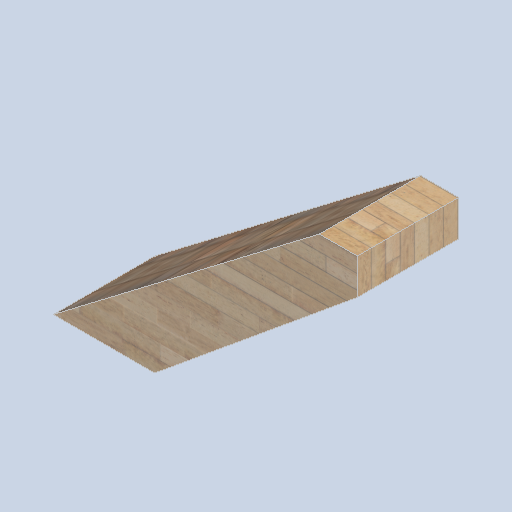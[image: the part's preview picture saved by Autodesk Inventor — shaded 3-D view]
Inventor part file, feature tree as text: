
AUTODESK INVENTOR PART (.ipt)
format: ipt  version: 2024.2 (Build 282272000, 272)  size: 160,256 bytes
history: native  units: in
note: dims shown in document units (in); Inventor stores cm internally (conversion verified against a paired STEP export)
features: other x3, sketch x1
ambient origin geometry x8: Origin, YZ Plane, XZ Plane, XY Plane, X Axis, Y Axis, Z Axis, Center Point
bodies: Body1 (feature_tree)
feature tree (4):
  other  "frame_rib_02.ipt"
  other  "Solid3::frame_rib_02.ipt"
  other  "TaggingFeature1"
  sketch  "Sketch1"  dims[d0=0.3937in]
